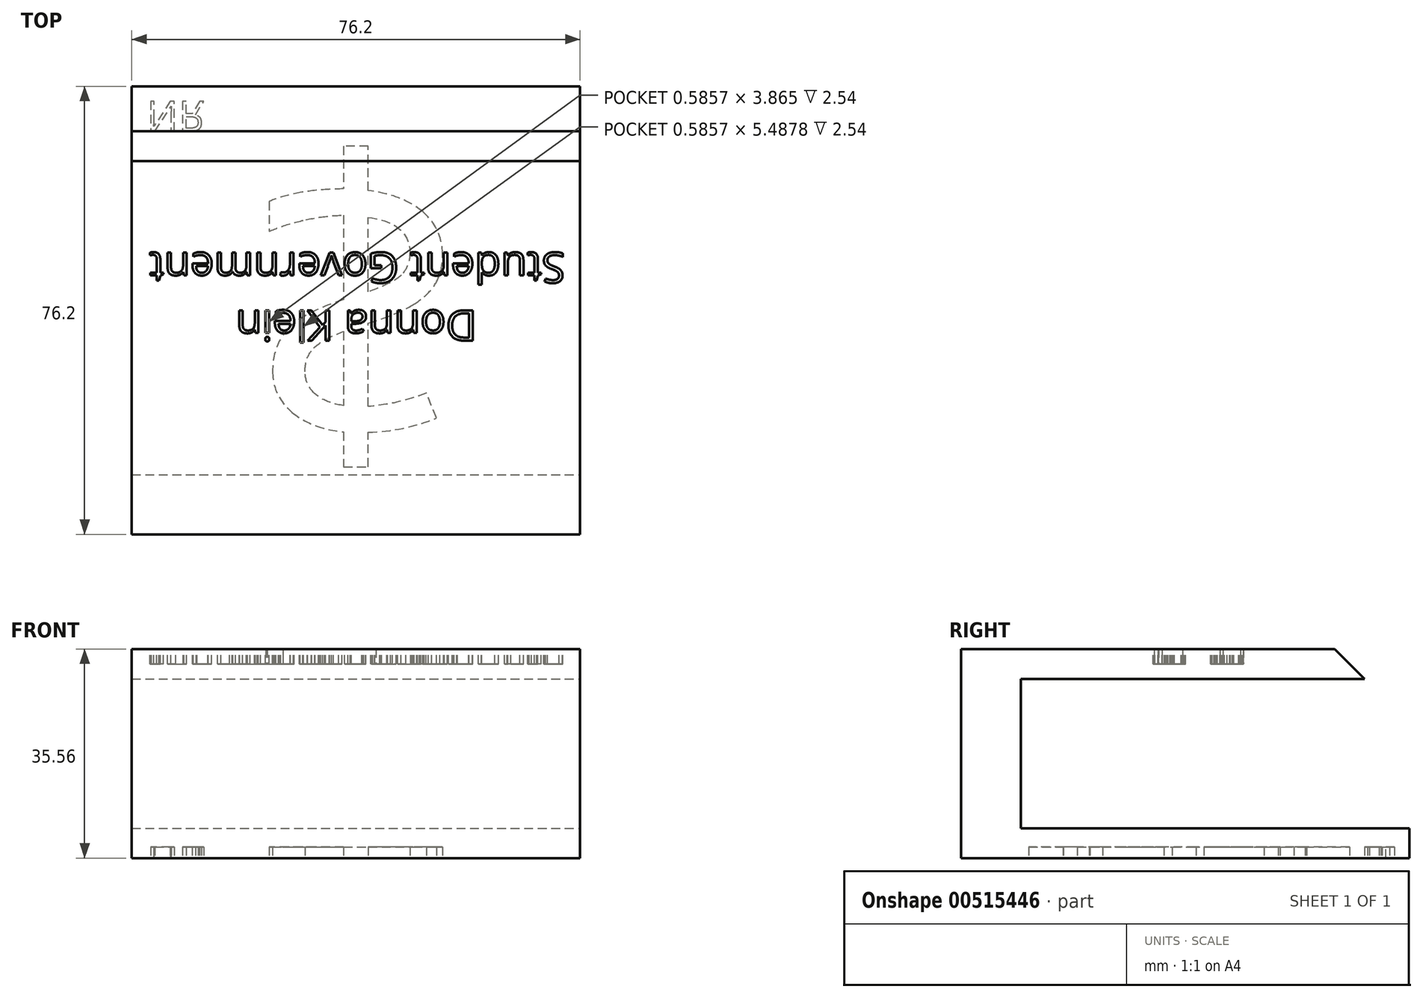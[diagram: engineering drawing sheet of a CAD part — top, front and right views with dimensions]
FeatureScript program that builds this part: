
annotation { "Feature Type Name" : "Feature", "Feature Type Description" : "" }
export const myFeature = defineFeature(function(context is Context, id is Id, definition is map)
    precondition{}
    {
        {
            var Q0;
            Q0=qCreatedBy(makeId("Top.planeOp"),FACE);
            var sketch = newSketch(context, id + "F0", { "sketchPlane" : qUnion([Q0])});
            skLineSegment(sketch, "E0.bottom", {"start": v(38.1, 38.1) * mm, "end": v(-38.1, 38.1) * mm});
            skLineSegment(sketch, "E0.top", {"start": v(38.1, -38.1) * mm, "end": v(-38.1, -38.1) * mm});
            skLineSegment(sketch, "E0.left", {"start": v(38.1, 38.1) * mm, "end": v(38.1, -38.1) * mm});
            skLineSegment(sketch, "E0.right", {"start": v(-38.1, 38.1) * mm, "end": v(-38.1, -38.1) * mm});
            skPoint(sketch, "E0.middle", {"position": v(0, 0) * mm});
            skSolve(sketch);
        }
        {
            var Q0;
            Q0=makeQuery(id+"F0.imprint","IMPRINT",FACE,{"disambiguationData":[TD([[makeQuery(id+"F0.imprint","IMPRINT",EDGE,{"derivedFrom":sQuery(id+"F0.wireOp",EDGE,"E0.bottom")}),1.0]])]});
            extrude(context, id + "F1", {"entities" : qUnion([Q0]), "depth" : 5.08 * mm, "offsetDistance" : 25.4 * mm});
        }
        {
            var Q0;
            Q0=makeQuery(id+"F1.opExtrude","CAP_FACE",FACE,{"disambiguationData":[OSD([sQuery(id+"F0.wireOp",EDGE,"E0.bottom"),sQuery(id+"F0.wireOp",EDGE,"E0.top"),sQuery(id+"F0.wireOp",EDGE,"E0.left"),sQuery(id+"F0.wireOp",EDGE,"E0.right")])],"isStart":false});
            var sketch = newSketch(context, id + "F2", { "sketchPlane" : qUnion([Q0])});
            skLineSegment(sketch, "E1.bottom", {"start": v(-38.1, -38.1) * mm, "end": v(38.1, -38.1) * mm});
            skLineSegment(sketch, "E1.top", {"start": v(-38.1, -27.94) * mm, "end": v(38.1, -27.94) * mm});
            skLineSegment(sketch, "E1.left", {"start": v(-38.1, -38.1) * mm, "end": v(-38.1, -27.94) * mm});
            skLineSegment(sketch, "E1.right", {"start": v(38.1, -38.1) * mm, "end": v(38.1, -27.94) * mm});
            skSolve(sketch);
        }
        {
            var Q0;
            Q0=makeQuery(id+"F2.imprint","IMPRINT",FACE,{"disambiguationData":[TD([[makeQuery(id+"F2.imprint","IMPRINT",EDGE,{"derivedFrom":sQuery(id+"F2.wireOp",EDGE,"E1.bottom")}),-1.0]])]});
            extrude(context, id + "F3", {"entities" : qUnion([Q0]), "operationType" : NewBodyOperationType.ADD, "depth" : 25.4 * mm, "offsetDistance" : 25.4 * mm});
        }
        {
            var Q0;
            Q0=makeQuery(id+"F3.opExtrude","CAP_FACE",FACE,{"disambiguationData":[OSD([sQuery(id+"F2.wireOp",EDGE,"E1.bottom"),sQuery(id+"F2.wireOp",EDGE,"E1.top"),sQuery(id+"F2.wireOp",EDGE,"E1.left"),sQuery(id+"F2.wireOp",EDGE,"E1.right")])],"isStart":false});
            var sketch = newSketch(context, id + "F4", { "sketchPlane" : qUnion([Q0])});
            skLineSegment(sketch, "E2.bottom", {"start": v(-38.1, -38.1) * mm, "end": v(38.1, -38.1) * mm});
            skLineSegment(sketch, "E2.top", {"start": v(-38.1, 38.1) * mm, "end": v(38.1, 38.1) * mm});
            skLineSegment(sketch, "E2.left", {"start": v(-38.1, -38.1) * mm, "end": v(-38.1, 38.1) * mm});
            skLineSegment(sketch, "E2.right", {"start": v(38.1, -38.1) * mm, "end": v(38.1, 38.1) * mm});
            skSolve(sketch);
        }
        {
            var Q0;
            {var subQ0=sQuery(id+"F4.wireOp",EDGE,"E2.top");Q0=makeQuery(id+"F4.imprint","IMPRINT",FACE,{"disambiguationData":[TD([[makeQuery(id+"F4.imprint","IMPRINT",EDGE,{"derivedFrom":subQ0}),-1.0]])]});}
            var Q1;
            {var subQ0=sQuery(id+"F4.wireOp",EDGE,"E2.bottom");Q1=makeQuery(id+"F4.imprint","IMPRINT",FACE,{"disambiguationData":[TD([[makeQuery(id+"F4.imprint","IMPRINT",EDGE,{"derivedFrom":subQ0}),-1.0]])]});}
            extrude(context, id + "F5", {"entities" : qUnion([Q0, Q1]), "operationType" : NewBodyOperationType.ADD, "depth" : 5.08 * mm, "offsetDistance" : 25.4 * mm});
        }
        {
            var Q0;
            Q0=makeQuery(id+"F5.opExtrude","CAP_EDGE",EDGE,{"disambiguationData":[OSD([sQuery(id+"F4.wireOp",EDGE,"E2.top")])],"isStart":false});
            chamfer(context, id + "F6", {"entities" : qUnion([Q0]), "width" : 12.7 * mm, "tangentPropagation" : true});
        }
        {
            var Q0;
            Q0=makeQuery(id+"F5.opExtrude","CAP_FACE",FACE,{"disambiguationData":[OSD([sQuery(id+"F4.wireOp",EDGE,"E2.bottom"),sQuery(id+"F4.wireOp",EDGE,"E2.top"),sQuery(id+"F4.wireOp",EDGE,"E2.left"),sQuery(id+"F4.wireOp",EDGE,"E2.right")])],"isStart":false});
            var sketch = newSketch(context, id + "F7", { "sketchPlane" : qUnion([Q0])});
            skText(sketch, "E3", { "text": "        Donna Klein        \nStudent Government", "fontName": "OpenSans-Regular.ttf"});
            skPoint(sketch, "E4", {"position": v(38.1, -6.35) * mm});
            const initialGuessF7  = {"E3": [0.03556, 0, -1, 0, 0.0052]};
            skSetInitialGuess(sketch, initialGuessF7);
            skSolve(sketch);
        }
        {
            var Q0;
            Q0 = qSketchRegion(id + "F7", true);
            extrude(context, id + "F8", {"entities" : qUnion([Q0]), "operationType" : NewBodyOperationType.REMOVE, "oppositeDirection" : true, "depth" : 2.54 * mm, "offsetDistance" : 25.4 * mm});
        }
        {
            var Q0;
            Q0=makeQuery(id+"F1.opExtrude","CAP_FACE",FACE,{"disambiguationData":[OSD([sQuery(id+"F0.wireOp",EDGE,"E0.bottom"),sQuery(id+"F0.wireOp",EDGE,"E0.top"),sQuery(id+"F0.wireOp",EDGE,"E0.left"),sQuery(id+"F0.wireOp",EDGE,"E0.right")])],"isStart":true});
            var sketch = newSketch(context, id + "F9", { "sketchPlane" : qUnion([Q0])});
            skText(sketch, "E5", { "text": "$", "fontName": "OpenSans-Regular.ttf"});
            skText(sketch, "E6", { "text": "NR", "fontName": "OpenSans-Regular.ttf"});
            const initialGuessF9  = {"E5": [-0.01905, -0.02403, 1, 0, 0.04806], "E6": [-0.03556, -0.03556, 1, 0, 0.00515]};
            skSetInitialGuess(sketch, initialGuessF9);
            skSolve(sketch);
        }
        {
            var Q0;
            Q0 = qSketchRegion(id + "F9", true);
            extrude(context, id + "F10", {"entities" : qUnion([Q0]), "operationType" : NewBodyOperationType.REMOVE, "oppositeDirection" : true, "depth" : 1.9 * mm, "offsetDistance" : 25.4 * mm});
        }
    });
